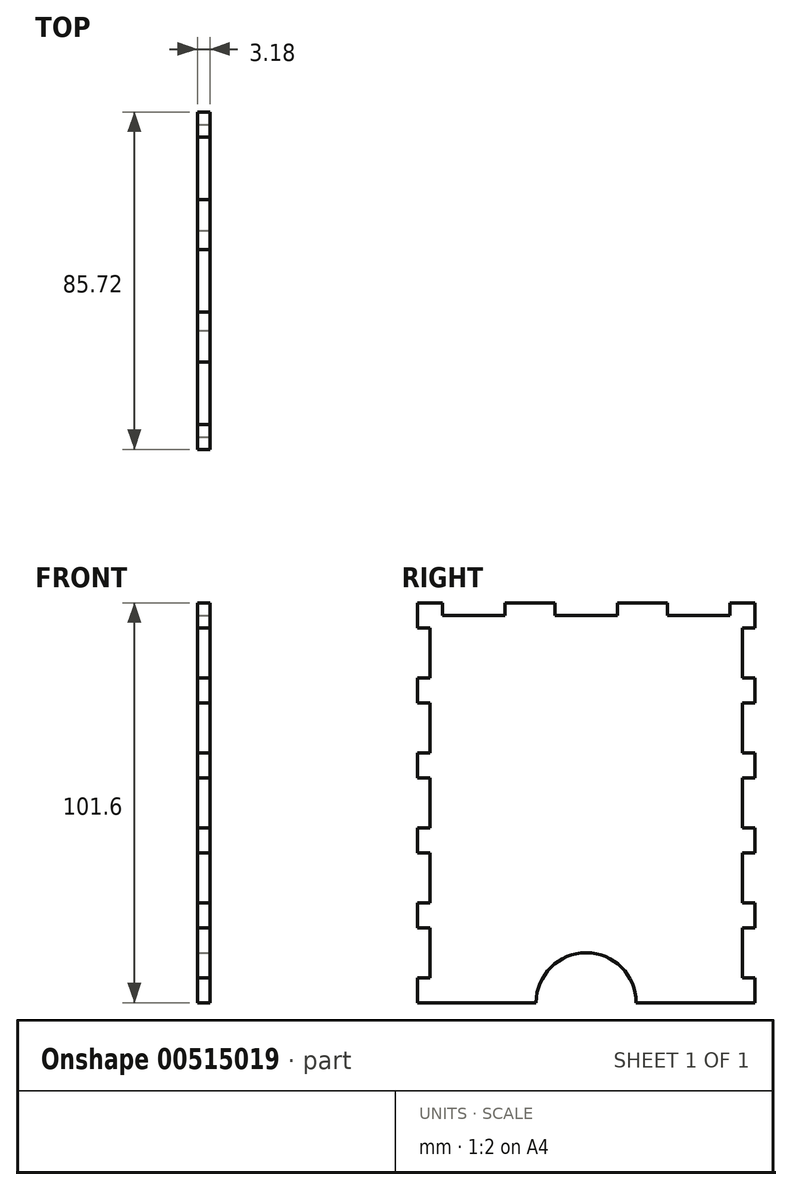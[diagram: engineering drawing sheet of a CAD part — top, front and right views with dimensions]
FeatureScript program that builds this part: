
annotation { "Feature Type Name" : "Feature", "Feature Type Description" : "" }
export const myFeature = defineFeature(function(context is Context, id is Id, definition is map)
    precondition{}
    {
        {
            var Q0;
            Q0=qCreatedBy(makeId("Right.planeOp"),FACE);
            var sketch = newSketch(context, id + "F0", { "sketchPlane" : qUnion([Q0])});
            skLineSegment(sketch, "E0.bottom", {"start": v(-42.86, 50.8) * mm, "end": v(42.86, 50.8) * mm});
            skLineSegment(sketch, "E0.top", {"start": v(-42.86, -50.8) * mm, "end": v(42.86, -50.8) * mm});
            skLineSegment(sketch, "E0.left", {"start": v(-42.86, 50.8) * mm, "end": v(-42.86, -50.8) * mm});
            skLineSegment(sketch, "E0.right", {"start": v(42.86, 50.8) * mm, "end": v(42.86, -50.8) * mm});
            skSolve(sketch);
        }
        {
            var Q0;
            Q0=qSketchRegion(id+"F0",true);
            extrude(context, id + "F1", {"entities" : qUnion([Q0]), "depth" : 3.17 * mm, "offsetDistance" : 25.4 * mm});
        }
        {
            var Q0;
            Q0=makeQuery(id+"F1.opExtrude","CAP_FACE",FACE,{"disambiguationData":[OSD([sQuery(id+"F0.wireOp",EDGE,"E0.bottom"),sQuery(id+"F0.wireOp",EDGE,"E0.top"),sQuery(id+"F0.wireOp",EDGE,"E0.left"),sQuery(id+"F0.wireOp",EDGE,"E0.right")])],"isStart":false});
            var sketch = newSketch(context, id + "F2", { "sketchPlane" : qUnion([Q0])});
            skLineSegment(sketch, "E1.bottom", {"start": v(-42.86, -44.45) * mm, "end": v(-39.69, -44.45) * mm});
            skLineSegment(sketch, "E1.top", {"start": v(-42.86, -31.75) * mm, "end": v(-39.69, -31.75) * mm});
            skLineSegment(sketch, "E1.left", {"start": v(-42.86, -44.45) * mm, "end": v(-42.86, -31.75) * mm});
            skLineSegment(sketch, "E1.right", {"start": v(-39.69, -44.45) * mm, "end": v(-39.69, -31.75) * mm});
            skLineSegment(sketch, "E2.0.1.0", {"start": v(-39.69, -25.4) * mm, "end": v(-39.69, -12.7) * mm});
            skLineSegment(sketch, "E2.0.1.1", {"start": v(-42.86, -25.4) * mm, "end": v(-42.86, -12.7) * mm});
            skLineSegment(sketch, "E2.0.1.2", {"start": v(-42.86, -12.7) * mm, "end": v(-39.69, -12.7) * mm});
            skLineSegment(sketch, "E2.0.1.3", {"start": v(-42.86, -25.4) * mm, "end": v(-39.69, -25.4) * mm});
            skLineSegment(sketch, "E2.0.2.0", {"start": v(-39.69, -6.35) * mm, "end": v(-39.69, 6.35) * mm});
            skLineSegment(sketch, "E2.0.2.1", {"start": v(-42.86, -6.35) * mm, "end": v(-42.86, 6.35) * mm});
            skLineSegment(sketch, "E2.0.2.2", {"start": v(-42.86, 6.35) * mm, "end": v(-39.69, 6.35) * mm});
            skLineSegment(sketch, "E2.0.2.3", {"start": v(-42.86, -6.35) * mm, "end": v(-39.69, -6.35) * mm});
            skLineSegment(sketch, "E2.0.3.0", {"start": v(-39.69, 12.7) * mm, "end": v(-39.69, 25.4) * mm});
            skLineSegment(sketch, "E2.0.3.1", {"start": v(-42.86, 12.7) * mm, "end": v(-42.86, 25.4) * mm});
            skLineSegment(sketch, "E2.0.3.2", {"start": v(-42.86, 25.4) * mm, "end": v(-39.69, 25.4) * mm});
            skLineSegment(sketch, "E2.0.3.3", {"start": v(-42.86, 12.7) * mm, "end": v(-39.69, 12.7) * mm});
            skLineSegment(sketch, "E2.direction1", {"start": v(-42.86, -44.45) * mm, "end": v(-17.46, -44.45) * mm, "construction": true});
            skLineSegment(sketch, "E2.direction2", {"start": v(-42.86, -44.45) * mm, "end": v(-42.86, -25.4) * mm, "construction": true});
            skLineSegment(sketch, "E3.0.0.4", {"start": v(-39.69, 31.75) * mm, "end": v(-39.69, 44.45) * mm});
            skLineSegment(sketch, "E3.3.0.4", {"start": v(-42.86, 31.75) * mm, "end": v(-42.86, 44.45) * mm});
            skLineSegment(sketch, "E3.6.0.4", {"start": v(-42.86, 44.45) * mm, "end": v(-39.69, 44.45) * mm});
            skLineSegment(sketch, "E3.9.0.4", {"start": v(-42.86, 31.75) * mm, "end": v(-39.69, 31.75) * mm});
            skLineSegment(sketch, "E4", {"start": v(0, 50.8) * mm, "end": v(0, -50.8) * mm, "construction": true});
            skLineSegment(sketch, "E5.MirrorCS", {"start": v(42.86, -44.45) * mm, "end": v(39.69, -44.45) * mm});
            skLineSegment(sketch, "E6.MirrorCS", {"start": v(42.86, -25.4) * mm, "end": v(39.69, -25.4) * mm});
            skLineSegment(sketch, "E7.MirrorCS", {"start": v(42.86, 31.75) * mm, "end": v(39.69, 31.75) * mm});
            skLineSegment(sketch, "E8.MirrorCS", {"start": v(42.86, 12.7) * mm, "end": v(39.69, 12.7) * mm});
            skLineSegment(sketch, "E9.MirrorCS", {"start": v(42.86, -31.75) * mm, "end": v(39.69, -31.75) * mm});
            skLineSegment(sketch, "E10.MirrorCS", {"start": v(42.86, 25.4) * mm, "end": v(39.69, 25.4) * mm});
            skLineSegment(sketch, "E11.MirrorCS", {"start": v(42.86, -12.7) * mm, "end": v(39.69, -12.7) * mm});
            skLineSegment(sketch, "E12.MirrorCS", {"start": v(42.86, 6.35) * mm, "end": v(39.69, 6.35) * mm});
            skLineSegment(sketch, "E13.MirrorCS", {"start": v(42.86, 44.45) * mm, "end": v(39.69, 44.45) * mm});
            skLineSegment(sketch, "E14.MirrorCS", {"start": v(42.86, -6.35) * mm, "end": v(39.69, -6.35) * mm});
            skLineSegment(sketch, "E15.MirrorCS", {"start": v(42.86, -44.45) * mm, "end": v(42.86, -31.75) * mm});
            skLineSegment(sketch, "E16.MirrorCS", {"start": v(39.69, 31.75) * mm, "end": v(39.69, 44.45) * mm});
            skLineSegment(sketch, "E17.MirrorCS", {"start": v(42.86, -25.4) * mm, "end": v(42.86, -12.7) * mm});
            skLineSegment(sketch, "E18.MirrorCS", {"start": v(39.69, -25.4) * mm, "end": v(39.69, -12.7) * mm});
            skLineSegment(sketch, "E19.MirrorCS", {"start": v(42.86, 12.7) * mm, "end": v(42.86, 25.4) * mm});
            skLineSegment(sketch, "E20.MirrorCS", {"start": v(42.86, -6.35) * mm, "end": v(42.86, 6.35) * mm});
            skLineSegment(sketch, "E21.MirrorCS", {"start": v(39.69, -44.45) * mm, "end": v(39.69, -31.75) * mm});
            skLineSegment(sketch, "E22.MirrorCS", {"start": v(39.69, -6.35) * mm, "end": v(39.69, 6.35) * mm});
            skLineSegment(sketch, "E23.MirrorCS", {"start": v(42.86, -44.45) * mm, "end": v(42.86, -25.4) * mm, "construction": true});
            skLineSegment(sketch, "E24.MirrorCS", {"start": v(39.69, 12.7) * mm, "end": v(39.69, 25.4) * mm});
            skLineSegment(sketch, "E25.MirrorCS", {"start": v(42.86, 31.75) * mm, "end": v(42.86, 44.45) * mm});
            skSolve(sketch);
        }
        {
            var Q0;
            Q0=qSketchRegion(id+"F2",true);
            extrude(context, id + "F3", {"entities" : qUnion([Q0]), "operationType" : NewBodyOperationType.REMOVE, "endBound" : BoundingType.THROUGH_ALL, "oppositeDirection" : true, "depth" : 25.4 * mm, "offsetDistance" : 25.4 * mm});
        }
        {
            var Q0;
            Q0=makeQuery(id+"F1.opExtrude","CAP_FACE",FACE,{"disambiguationData":[OSD([sQuery(id+"F0.wireOp",EDGE,"E0.bottom"),sQuery(id+"F0.wireOp",EDGE,"E0.top"),sQuery(id+"F0.wireOp",EDGE,"E0.left"),sQuery(id+"F0.wireOp",EDGE,"E0.right")])],"isStart":false});
            var sketch = newSketch(context, id + "F4", { "sketchPlane" : qUnion([Q0])});
            skLineSegment(sketch, "E26.bottom", {"start": v(-36.51, 50.8) * mm, "end": v(-20.64, 50.8) * mm});
            skLineSegment(sketch, "E26.top", {"start": v(-36.51, 47.62) * mm, "end": v(-20.64, 47.62) * mm});
            skLineSegment(sketch, "E26.left", {"start": v(-36.51, 50.8) * mm, "end": v(-36.51, 47.62) * mm});
            skLineSegment(sketch, "E26.right", {"start": v(-20.64, 50.8) * mm, "end": v(-20.64, 47.62) * mm});
            skLineSegment(sketch, "E27.1.0.0", {"start": v(-7.94, 50.8) * mm, "end": v(7.94, 50.8) * mm});
            skLineSegment(sketch, "E27.1.0.1", {"start": v(-7.94, 47.62) * mm, "end": v(7.94, 47.62) * mm});
            skLineSegment(sketch, "E27.1.0.2", {"start": v(7.94, 50.8) * mm, "end": v(7.94, 47.62) * mm});
            skLineSegment(sketch, "E27.1.0.3", {"start": v(-7.94, 50.8) * mm, "end": v(-7.94, 47.62) * mm});
            skLineSegment(sketch, "E27.2.0.0", {"start": v(20.64, 50.8) * mm, "end": v(36.51, 50.8) * mm});
            skLineSegment(sketch, "E27.2.0.1", {"start": v(20.64, 47.62) * mm, "end": v(36.51, 47.62) * mm});
            skLineSegment(sketch, "E27.2.0.2", {"start": v(36.51, 50.8) * mm, "end": v(36.51, 47.62) * mm});
            skLineSegment(sketch, "E27.2.0.3", {"start": v(20.64, 50.8) * mm, "end": v(20.64, 47.62) * mm});
            skLineSegment(sketch, "E27.direction1", {"start": v(-36.51, 47.62) * mm, "end": v(-7.94, 47.62) * mm, "construction": true});
            skSolve(sketch);
        }
        {
            var Q0;
            Q0=qSketchRegion(id+"F4",true);
            extrude(context, id + "F5", {"entities" : qUnion([Q0]), "operationType" : NewBodyOperationType.REMOVE, "endBound" : BoundingType.THROUGH_ALL, "oppositeDirection" : true, "depth" : 25.4 * mm, "offsetDistance" : 25.4 * mm});
        }
        {
            var Q0;
            Q0=makeQuery(id+"F1.opExtrude","CAP_FACE",FACE,{"disambiguationData":[OSD([sQuery(id+"F0.wireOp",EDGE,"E0.bottom"),sQuery(id+"F0.wireOp",EDGE,"E0.top"),sQuery(id+"F0.wireOp",EDGE,"E0.left"),sQuery(id+"F0.wireOp",EDGE,"E0.right")])],"isStart":false});
            var sketch = newSketch(context, id + "F6", { "sketchPlane" : qUnion([Q0])});
            skEllipse(sketch, "E28", {"center": v(0, -50.8) * mm, "majorRadius": 12.7 * mm, "minorRadius": 12.7 * mm, "majorAxis": v(1, 0)});
            skSolve(sketch);
        }
        {
            var Q0;
            Q0 = qSketchRegion(id + "F6", true);
            extrude(context, id + "F7", {"entities" : qUnion([Q0]), "operationType" : NewBodyOperationType.REMOVE, "endBound" : BoundingType.THROUGH_ALL, "oppositeDirection" : true, "depth" : 25.4 * mm, "offsetDistance" : 25.4 * mm});
        }
    });
